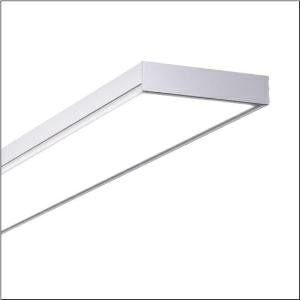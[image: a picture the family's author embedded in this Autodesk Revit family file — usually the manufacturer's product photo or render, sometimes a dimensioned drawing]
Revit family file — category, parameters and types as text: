
# Revit family: apollon_r__31_surface_51mp26wd2441ea_40fe
name_source: partatom
category: Lighting Fixtures
units: mm (PartAtom-declared; Revit-internal decimal feet)

## family parameters
Cut with Voids When Loaded = No
Host = Face
Light Source = No
Part Type = Normal
Room Calculation Point = No
Round Connector Dimension = Use Diameter
Shared = No

## types (1)
- Apollon® 31 Surface (1 x LED, 4600 lm, 33 W, 4000K)
    Apparent Load = 33 VA
    CIE Flux Codes = 61 87 97 97 100
    Color Rendering = 80
    Color Temperature = 4000K
    Default Elevation = 1800 mm
    Description = Apollon® 31 Surface, office luminaire, primary optical cover: micro prismatic cover, of PMMA, light emission: direct distribution, primary light characteristic: symmetric, installation type: surface-mounted, LED, rated luminous flux: 4.600lm, luminous efficacy: 139lm/W, light colour: 840, colour temperature: 4000K, control gear: ECG DALI, with terminal, 5-pole, mains connection: 220..240V, AC, 50/60Hz, rated input power: 33W, housing, of sheet steel, coil coated, metallic grey (RAL 9006), length: 1.545mm, width: 200mm, height: 44mm, protection rating (complete): IP20, insulation class (complete): insulation class II (safety insulation), certification: CE, impact resistance: IK02, permissible operating ambient temperature: -20..+40°C, standard: EN 60598-2-22, packaging unit: 1 piece
    Height = 44 mm
    Lamp = 1 x LED
    Lamp Light Flux = 4600 lm
    Lamp Power = 33 W
    Lamp count = 1
    Length = 1545 mm
    Luminous efficacy = 139 lm/W
    Manufacturer = Siteco
    ModVariant = No
    Model = 51MP26WD2441EA
    Mounting Place = Ceiling
    Mounting Type = Surface mounted
    Number of Poles = 1
    OnlyDefault = Yes
    Power Factor = 1
    Product Name = Apollon® 31 Surface
    Product group = office luminaire | ceiling mounted
    ProductGroupID = 300
    Protection Class = Protection class II
    Protection Degree = IP 20
    RLX_Detail_Level = 1
    RLX_Emergency_Light_Flux = 0 lm
    RLX_Emergency_Type = 0
    RLX_Emergency_Type_DB = No
    RlxData = <blob elided: 24105 chars, md5=a66d32d2>
    Socket = socket
    Standby Power = 0 W
    System Light Flux = 4600 lm
    System Power = 33 W
    Type Comments = Product without accessories
    Type Image = l_1313654.jpg
    URL = http://relux.com
    VarID = ---
    Voltage = 0 V
    Weight = 0.00 kg
    Width = 200 mm  [stored 0.656168 ft]

note: [stored X ft] marks values corroborated as IEEE doubles in the binary element streams (Revit-internal decimal feet)

## geometry (parser evidence)
native form markers: Blend x4, Sweep x9
no freeform markers — native parametric forms only
